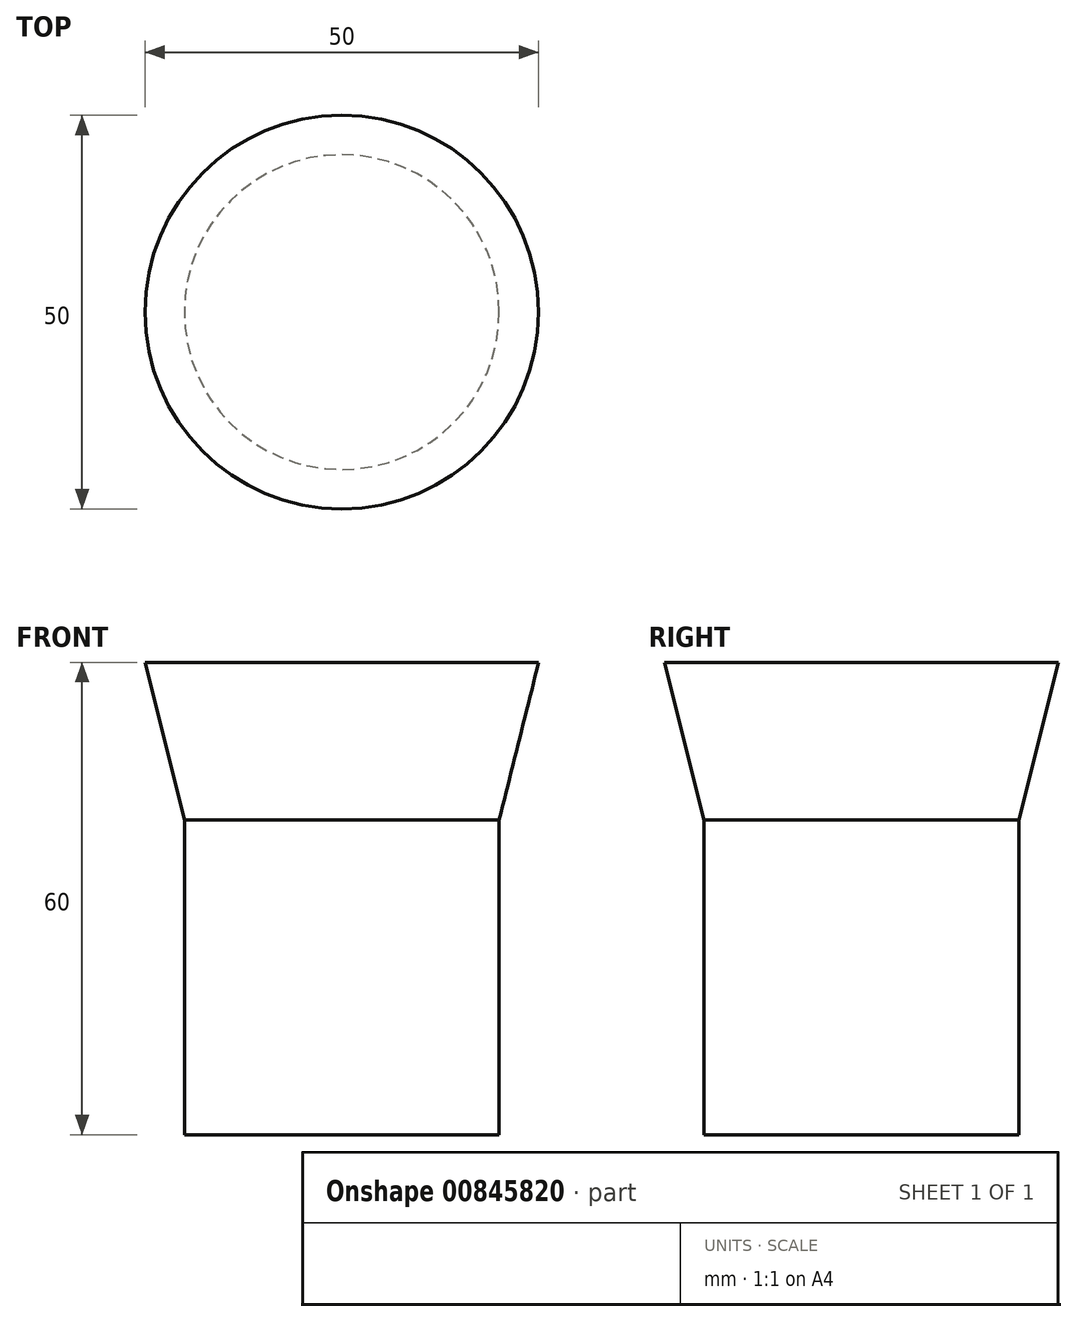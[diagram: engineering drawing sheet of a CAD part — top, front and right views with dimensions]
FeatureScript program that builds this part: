
annotation { "Feature Type Name" : "Feature", "Feature Type Description" : "" }
export const myFeature = defineFeature(function(context is Context, id is Id, definition is map)
    precondition{}
    {
        {
            var Q0;
            Q0=qCreatedBy(makeId("Top.planeOp"),FACE);
            var sketch = newSketch(context, id + "F0", { "sketchPlane" : qUnion([Q0])});
            skCircle(sketch, "E0", {"center": v(0, 0) * mm, "radius": 20 * mm});
            skSolve(sketch);
        }
        {
            var Q0;
            Q0=makeQuery(id+"F0.imprint","IMPRINT",FACE,{"disambiguationData":[TD([[makeQuery(id+"F0.imprint","IMPRINT",EDGE,{"derivedFrom":sQuery(id+"F0.wireOp",EDGE,"E0")}),1.0]])]});
            extrude(context, id + "F1", {"entities" : qUnion([Q0]), "depth" : 40 * mm, "offsetDistance" : 25 * mm});
        }
        {
            var Q0;
            Q0=qCreatedBy(makeId("Top.planeOp"),FACE);
            cPlane(context, id + "F2", {"entities" : qUnion([Q0]), "cplaneType" : CPlaneType.OFFSET, "offset" : 60 * mm, "width" : 150 * mm, "height" : 150 * mm});
        }
        {
            var Q0;
            Q0=qCreatedBy(id+"F2.planeOp",FACE);
            var sketch = newSketch(context, id + "F3", { "sketchPlane" : qUnion([Q0])});
            skCircle(sketch, "E1", {"center": v(0, 0) * mm, "radius": 25 * mm});
            skSolve(sketch);
        }
        {
            var Q1;
            Q1=makeQuery(id+"F3.imprint","IMPRINT",FACE,{"disambiguationData":[TD([[makeQuery(id+"F3.imprint","IMPRINT",EDGE,{"derivedFrom":sQuery(id+"F3.wireOp",EDGE,"E1")}),1.0]])]});
            var Q2;
            Q2=makeQuery(id+"F1.opExtrude","CAP_FACE",FACE,{"disambiguationData":[OSD([sQuery(id+"F0.wireOp",EDGE,"E0")])],"isStart":false});
            loft(context, id + "F4", {"operationType" : NewBodyOperationType.ADD, "sheetProfilesArray" : [{ "sheetProfileEntities" : qUnion([Q1]) }, { "sheetProfileEntities" : qUnion([Q2]) }]});
        }
    });
